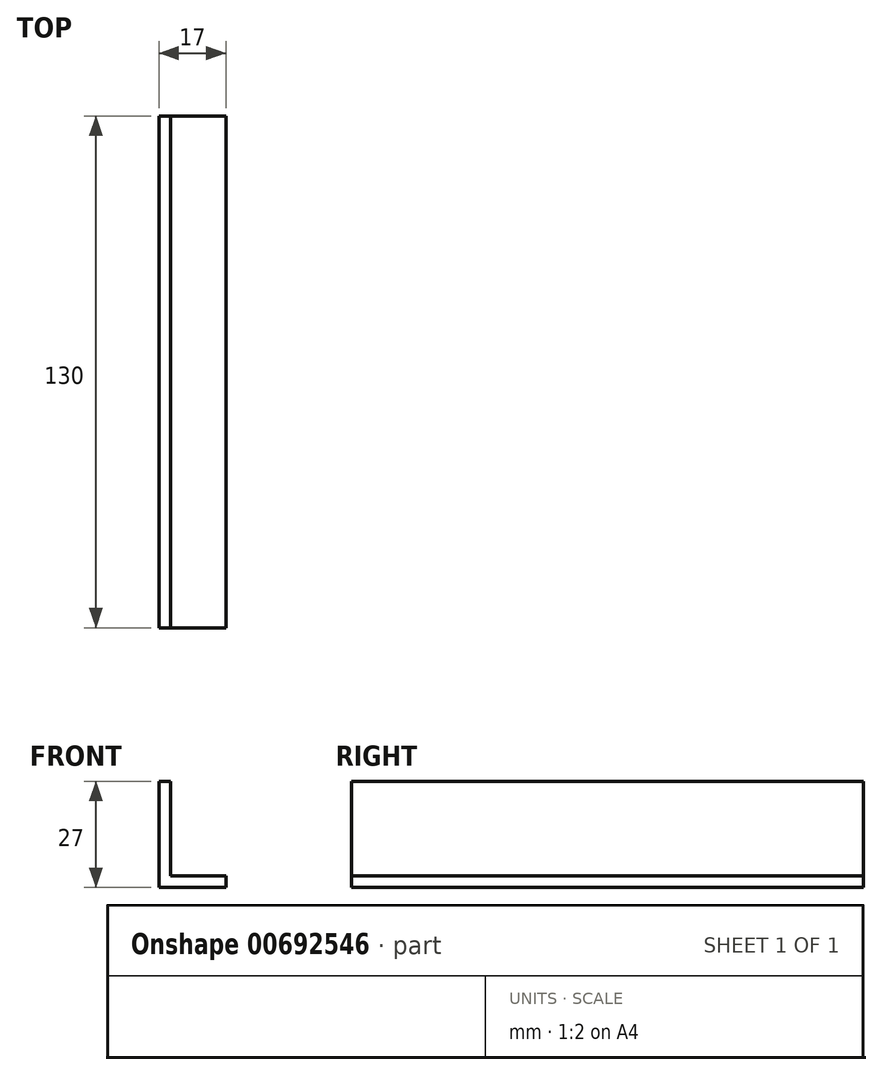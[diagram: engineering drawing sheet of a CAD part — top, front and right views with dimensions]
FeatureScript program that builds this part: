
annotation { "Feature Type Name" : "Feature", "Feature Type Description" : "" }
export const myFeature = defineFeature(function(context is Context, id is Id, definition is map)
    precondition{}
    {
        {
            var Q0;
            Q0=qCreatedBy(makeId("Front.planeOp"),FACE);
            var sketch = newSketch(context, id + "F0", { "sketchPlane" : qUnion([Q0])});
            skLineSegment(sketch, "E0", {"start": v(0, 0) * mm, "end": v(-17, 0) * mm});
            skLineSegment(sketch, "E1", {"start": v(-17, 0) * mm, "end": v(-17, 27) * mm});
            skLineSegment(sketch, "E2", {"start": v(-17, 27) * mm, "end": v(-14, 27) * mm});
            skLineSegment(sketch, "E3", {"start": v(-14, 27) * mm, "end": v(-14, 3) * mm});
            skLineSegment(sketch, "E4", {"start": v(-14, 3) * mm, "end": v(0, 3) * mm});
            skLineSegment(sketch, "E5", {"start": v(0, 3) * mm, "end": v(0, 0) * mm});
            skSolve(sketch);
        }
        {
            var Q0;
            Q0 = qSketchRegion(id + "F0", true);
            extrude(context, id + "F1", {"entities" : qUnion([Q0]), "depth" : 130 * mm, "offsetDistance" : 25 * mm});
        }
    });
